# Revit family: LED COB INGROUND 12W_LKP0128WW.55
name_source: partatom
category: Luminarias
units: mm (PartAtom-declared; Revit-internal decimal feet)

## family parameters
Compartido = No
Corte con vacíos al cargar = No
Cota de conector redondo = Diámetro de uso
Origen de luz = Sí
Punto de cálculo de habitación = No
Se basa en plano de trabajo = Sí
Siempre vertical = No
Tipo de pieza = Normal

## types (1)
- EMP_LKP0128WW.55
    Cambio de temperatura de color de luz atenuada = <Ninguno>
    Comentarios de vataje = 100-277V
    Descripción = LUMINARIA TIPO CIRCULAR PARA EMPOTRAR EN PISO CON CUERPO DE ALUMINIO FUNDIDO A PRESION CUBIERTO CON POLVO GRIS OSCURO, CON CUBIERTA DE ACERO INOXIDABLE Y VIDRIO TEMPLADO DE 8MM, HOUSING TIPO ABS DE 155MM DE DIAMETRO Y 220MM DE PROFUNDO. CUENTA CON 12 LED COB TIPO NICHIA CON UNA POTENCIA TOTAL DE 14W, A UNA TEMPERATURA EN BLANCO CALIDO 3000K CON 1230 LUMENES, 102mA EN CORRIENTE DE OPERACIÓN, IP67, IK10, IRC 80, APERTURA EN 55 GRADOS POR PROYECTO, ALIMENTADA A 100-277V
    Elevación por defecto = 0 mm  [stored 0 ft]
    Fabricante = BRILLANT
    Filtro de color = 16777215
    Longitud de símbolo de origen de luz = 500 mm  [stored 1.64042 ft]
    Lámpara = NICHIA
    Modelo = LKP0128WW.55
    Watt per fixture = 14
    Ángulo de campo de foco = 55.00°
    Ángulo de enfoque = 55.00°
    Ángulo de inclinación = 105.00°

note: [stored X ft] marks values corroborated as IEEE doubles in the binary element streams (Revit-internal decimal feet)

## geometry (parser evidence)
native form markers: Blend x2
no freeform markers — native parametric forms only
